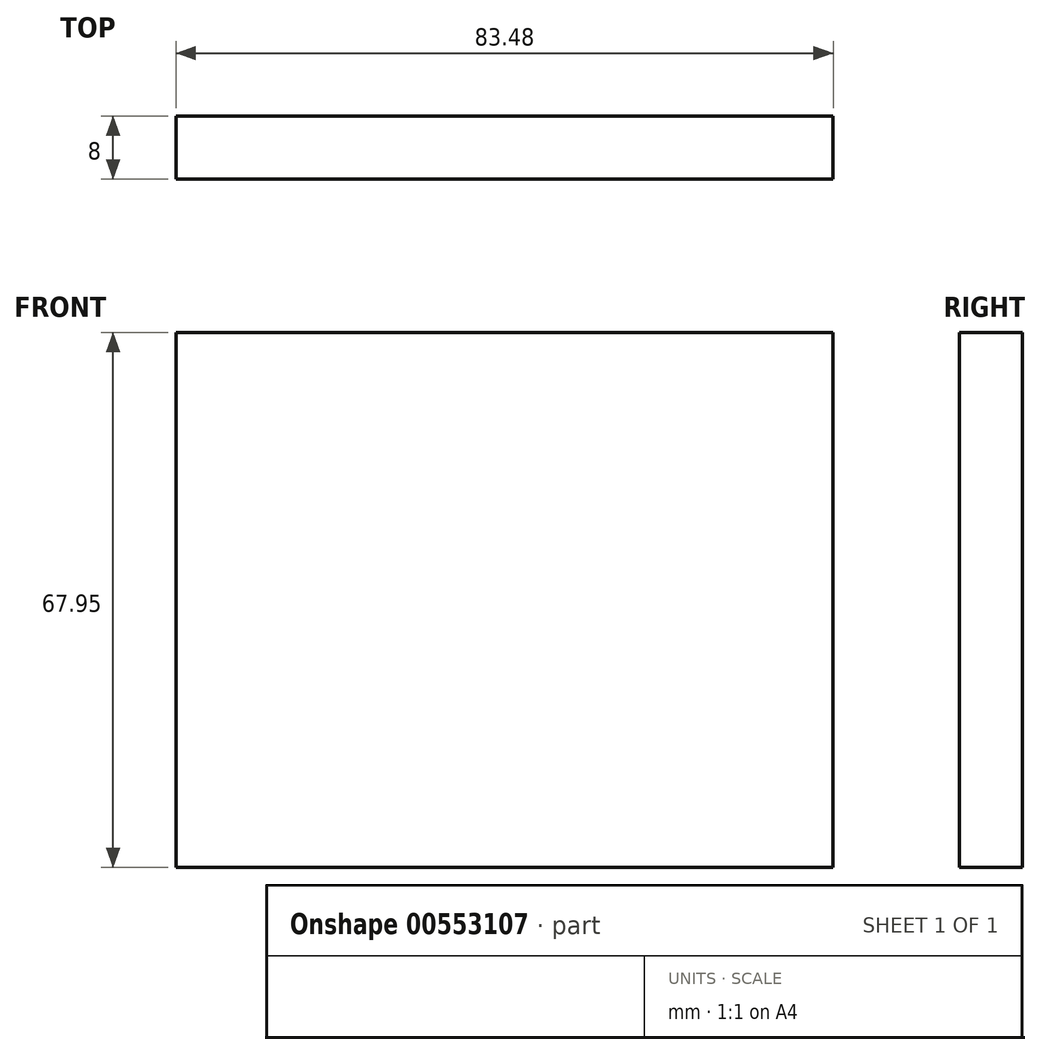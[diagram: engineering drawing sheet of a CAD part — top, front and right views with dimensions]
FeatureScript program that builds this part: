
annotation { "Feature Type Name" : "Feature", "Feature Type Description" : "" }
export const myFeature = defineFeature(function(context is Context, id is Id, definition is map)
    precondition{}
    {
        {
            var Q0;
            Q0=qCreatedBy(makeId("Front.planeOp"),FACE);
            var sketch = newSketch(context, id + "F0", { "sketchPlane" : qUnion([Q0])});
            skLineSegment(sketch, "E0.bottom", {"start": v(-38.2, 26.61) * mm, "end": v(45.28, 26.61) * mm});
            skLineSegment(sketch, "E0.top", {"start": v(-38.2, -41.34) * mm, "end": v(45.28, -41.34) * mm});
            skLineSegment(sketch, "E0.left", {"start": v(-38.2, 26.61) * mm, "end": v(-38.2, -41.34) * mm});
            skLineSegment(sketch, "E0.right", {"start": v(45.28, 26.61) * mm, "end": v(45.28, -41.34) * mm});
            skSolve(sketch);
        }
        {
            var Q0;
            Q0 = qSketchRegion(id + "F0", true);
            extrude(context, id + "F1", {"entities" : qUnion([Q0]), "depth" : 68 * mm, "offsetDistance" : 25 * mm});
        }
        {
            var Q0;
            Q0=makeQuery(id+"F1.opExtrude","CAP_FACE",FACE,{"disambiguationData":[OSD([sQuery(id+"F0.wireOp",EDGE,"E0.bottom"),sQuery(id+"F0.wireOp",EDGE,"E0.top"),sQuery(id+"F0.wireOp",EDGE,"E0.left"),sQuery(id+"F0.wireOp",EDGE,"E0.right")])],"isStart":false});
            extrude(context, id + "F2", {"entities" : qUnion([Q0]), "operationType" : NewBodyOperationType.INTERSECT, "oppositeDirection" : true, "depth" : 8 * mm, "offsetDistance" : 25 * mm});
        }
    });
